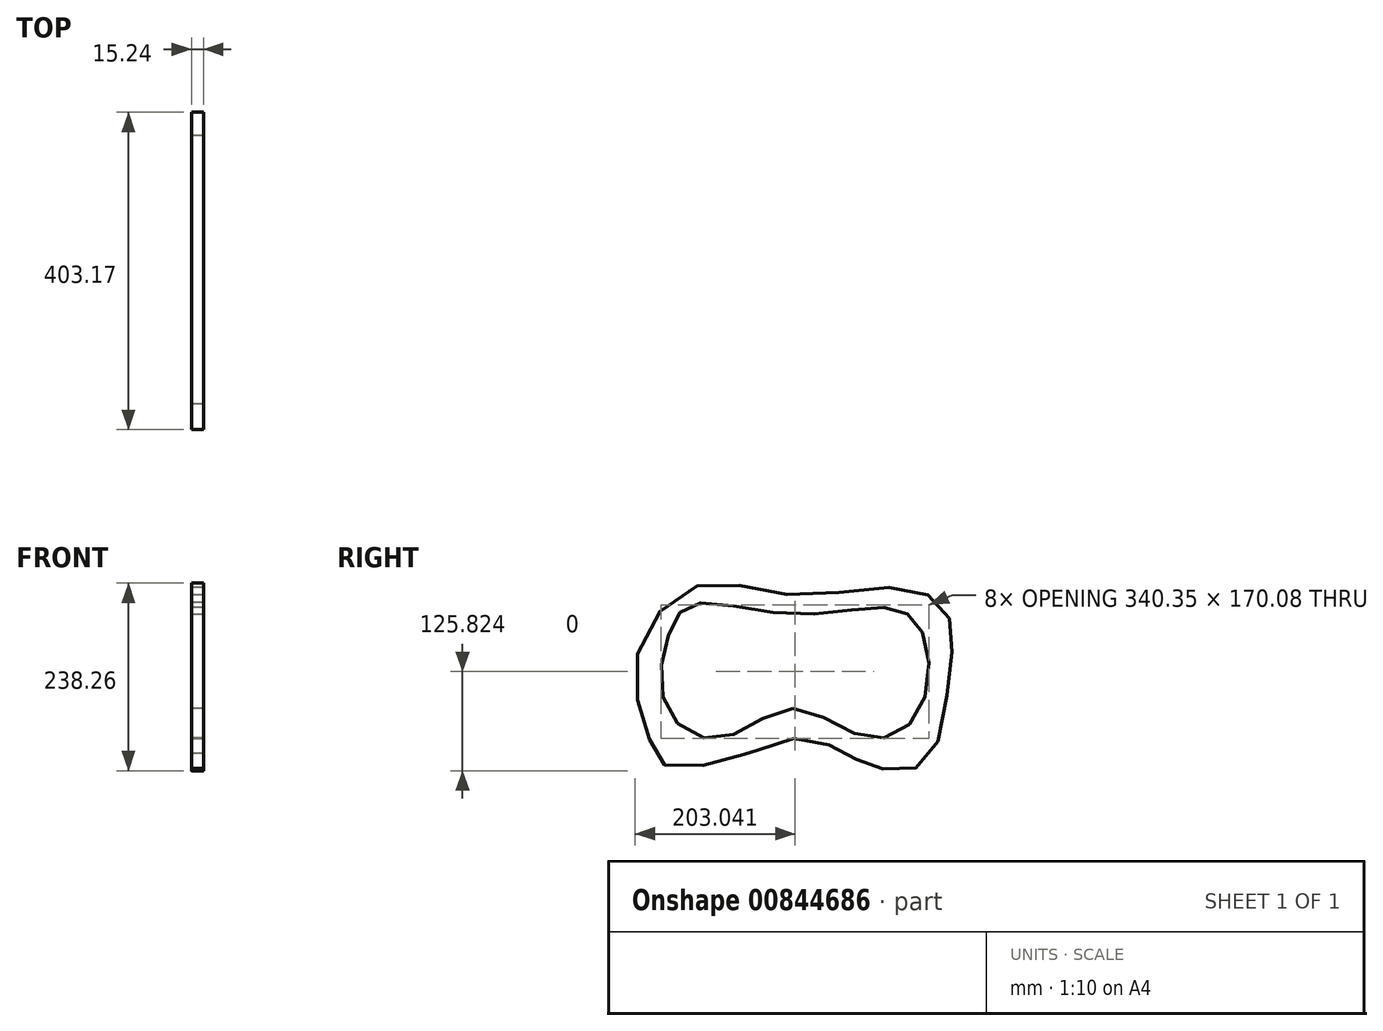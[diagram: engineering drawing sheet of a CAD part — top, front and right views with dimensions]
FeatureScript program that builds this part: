
annotation { "Feature Type Name" : "Feature", "Feature Type Description" : "" }
export const myFeature = defineFeature(function(context is Context, id is Id, definition is map)
    precondition{}
    {
        {
            var Q0;
            Q0=qCreatedBy(makeId("Right.planeOp"),FACE);
            var sketch = newSketch(context, id + "F0", { "sketchPlane" : qUnion([Q0])});
            skLineSegment(sketch, "E0", {"start": v(-106.14, 103.5) * mm, "end": v(290.1, 103.5) * mm, "construction": true});
            skLineSegment(sketch, "E1", {"start": v(-106.14, 103.5) * mm, "end": v(-106.14, -125.1) * mm, "construction": true});
            skLineSegment(sketch, "E2", {"start": v(-106.14, -125.1) * mm, "end": v(290.1, -125.1) * mm, "construction": true});
            skLineSegment(sketch, "E3", {"start": v(290.1, -125.1) * mm, "end": v(290.1, 103.5) * mm, "construction": true});
            skLineSegment(sketch, "E4", {"start": v(91.98, -125.1) * mm, "end": v(91.98, -48.9) * mm, "construction": true});
            skCircle(sketch, "E5", {"center": v(91.98, -125.1) * mm, "radius": 76.2 * mm, "construction": true});
            skLineSegment(sketch, "E6", {"start": v(282.67, -125.1) * mm, "end": v(282.67, -87) * mm, "construction": true});
            skLineSegment(sketch, "E7", {"start": v(282.67, -87) * mm, "end": v(-64.81, -87) * mm, "construction": true});
            skLineSegment(sketch, "E8", {"start": v(91.98, 103.5) * mm, "end": v(91.98, 70.47) * mm, "construction": true});
            skLineSegment(sketch, "E9", {"start": v(290.1, -10.8) * mm, "end": v(254.54, -10.8) * mm, "construction": true});
            skLineSegment(sketch, "E10", {"start": v(-106.14, -10.8) * mm, "end": v(-68.04, -10.8) * mm, "construction": true});
            skLineSegment(sketch, "E11", {"start": v(91.98, 70.47) * mm, "end": v(256.16, 70.47) * mm, "construction": true});
            skLineSegment(sketch, "E12", {"start": v(254.54, -10.8) * mm, "end": v(256.16, 70.47) * mm, "construction": true});
            skLineSegment(sketch, "E13", {"start": v(-68.04, -10.8) * mm, "end": v(-68.04, -87) * mm, "construction": true});
            skLineSegment(sketch, "E14", {"start": v(91.98, 70.47) * mm, "end": v(-68.04, 70.47) * mm, "construction": true});
            skLineSegment(sketch, "E15", {"start": v(254.54, -10.8) * mm, "end": v(254.54, -87) * mm, "construction": true});
            skFitSpline(sketch, "E16", {"points": [v(91.98, -48.9) * mm, v(189.58, -87) * mm, v(254.54, -48.9) * mm, v(255.74, 49.2) * mm, v(214.46, 78.69) * mm, v(91.98, 70.47) * mm, v(-34.4, 83.46) * mm, v(-66.3, 42.93) * mm, v(-68.04, -48.9) * mm, v(0, -87) * mm, v(91.98, -48.9) * mm]});
            skFitSpline(sketch, "E17", {"points": [v(93.72, -87) * mm, v(159.16, -106.37) * mm, v(202.48, -125.1) * mm, v(261.47, -116.74) * mm, v(290.1, -10.8) * mm, v(290.1, 66.74) * mm, v(237.5, 103.5) * mm, v(91.98, 95.36) * mm, v(-28.75, 106.93) * mm, v(-106.14, 15.4) * mm, v(-88.72, -91.54) * mm, v(-58.3, -125.1) * mm, v(34.79, -106.37) * mm, v(37.55, -106.37) * mm, v(93.72, -87) * mm]});
            skSolve(sketch);
        }
        {
            var Q0;
            Q0=makeQuery(id+"F0.imprint","IMPRINT",FACE,{"disambiguationData":[TD([[makeQuery(id+"F0.imprint","IMPRINT",EDGE,{"derivedFrom":sQuery(id+"F0.wireOp",EDGE,"E16")}),-1.0]])]});
            extrude(context, id + "F1", {"entities" : qUnion([Q0]), "depth" : 15.24 * mm, "offsetDistance" : 25.4 * mm});
        }
    });
